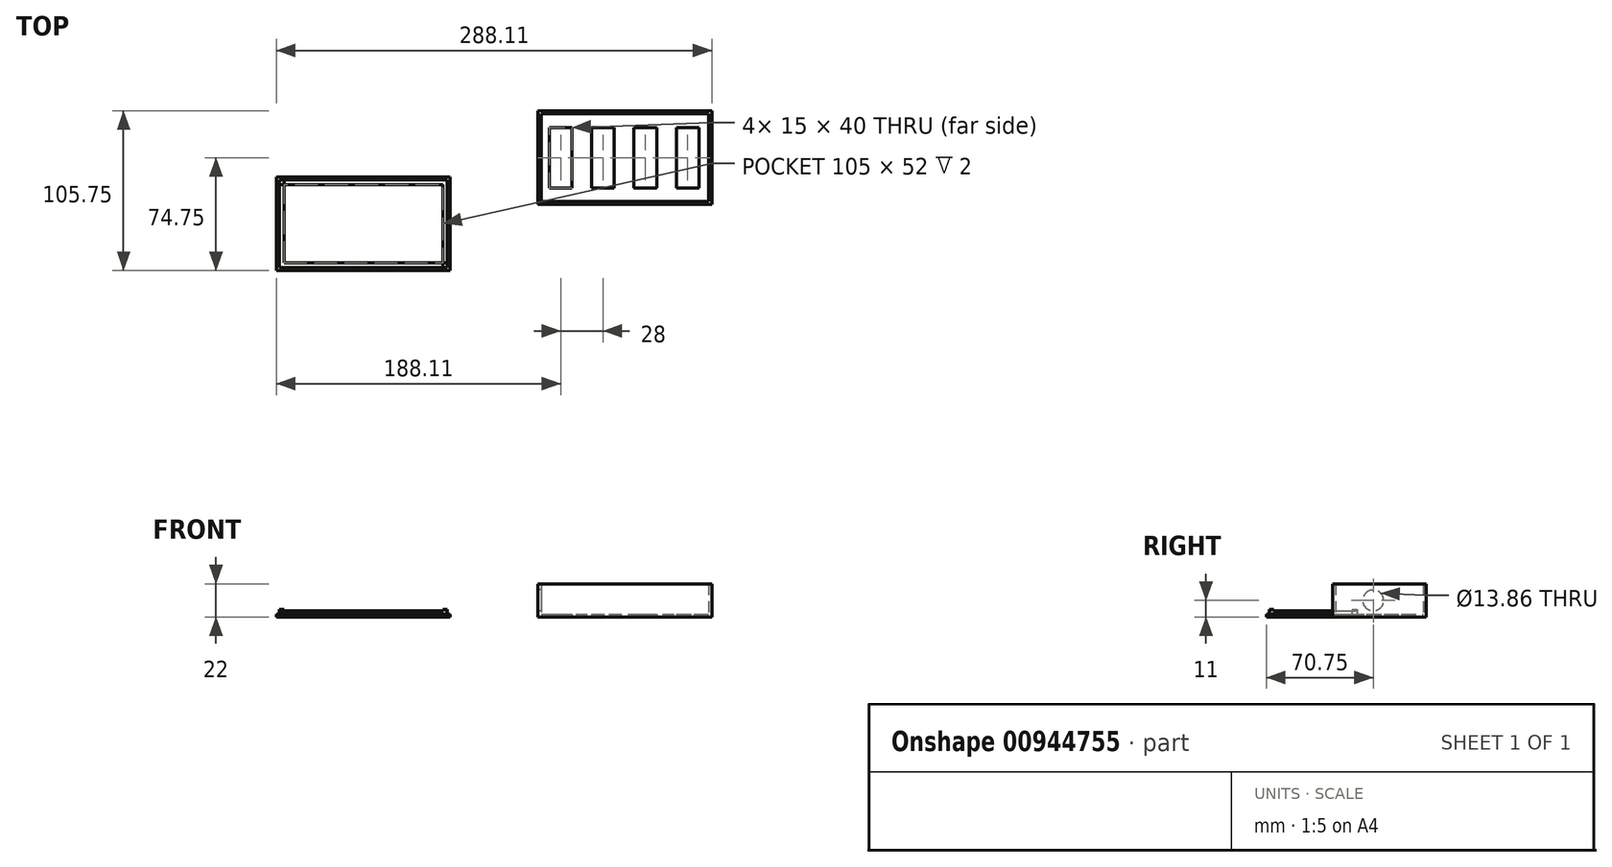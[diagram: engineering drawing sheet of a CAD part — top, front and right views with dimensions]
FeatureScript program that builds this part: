
annotation { "Feature Type Name" : "Feature", "Feature Type Description" : "" }
export const myFeature = defineFeature(function(context is Context, id is Id, definition is map)
    precondition{}
    {
        {
            var Q0;
            Q0=qCreatedBy(makeId("Top.planeOp"),FACE);
            var sketch = newSketch(context, id + "F0", { "sketchPlane" : qUnion([Q0])});
            skLineSegment(sketch, "E0.bottom", {"start": v(0, 0) * mm, "end": v(115, 0) * mm});
            skLineSegment(sketch, "E0.top", {"start": v(0, 62) * mm, "end": v(115, 62) * mm});
            skLineSegment(sketch, "E0.left", {"start": v(0, 0) * mm, "end": v(0, 62) * mm});
            skLineSegment(sketch, "E0.right", {"start": v(115, 0) * mm, "end": v(115, 62) * mm});
            skLineSegment(sketch, "E1.0", {"start": v(2, 2) * mm, "end": v(2, 60) * mm});
            skLineSegment(sketch, "E1.1", {"start": v(2, 2) * mm, "end": v(113, 2) * mm});
            skLineSegment(sketch, "E1.2", {"start": v(113, 2) * mm, "end": v(113, 60) * mm});
            skLineSegment(sketch, "E1.3", {"start": v(2, 60) * mm, "end": v(113, 60) * mm});
            skLineSegment(sketch, "E2.bottom", {"start": v(7.5, 11) * mm, "end": v(22.5, 11) * mm});
            skLineSegment(sketch, "E2.top", {"start": v(7.5, 51) * mm, "end": v(22.5, 51) * mm});
            skLineSegment(sketch, "E2.left", {"start": v(7.5, 11) * mm, "end": v(7.5, 51) * mm});
            skLineSegment(sketch, "E2.right", {"start": v(22.5, 11) * mm, "end": v(22.5, 51) * mm});
            skPoint(sketch, "E2.middle", {"position": v(15, 31) * mm});
            skPoint(sketch, "E2.middle.positionSnap0", {"position": v(2, 31) * mm});
            skPoint(sketch, "E2.centerSnap0", {"position": v(2, 31) * mm});
            skLineSegment(sketch, "E3.1.0.0", {"start": v(50.5, 11) * mm, "end": v(50.5, 51) * mm});
            skLineSegment(sketch, "E3.1.0.1", {"start": v(35.5, 11) * mm, "end": v(50.5, 11) * mm});
            skLineSegment(sketch, "E3.1.0.2", {"start": v(35.5, 11) * mm, "end": v(35.5, 51) * mm});
            skLineSegment(sketch, "E3.1.0.3", {"start": v(35.5, 51) * mm, "end": v(50.5, 51) * mm});
            skLineSegment(sketch, "E3.2.0.0", {"start": v(78.5, 11) * mm, "end": v(78.5, 51) * mm});
            skLineSegment(sketch, "E3.2.0.1", {"start": v(63.5, 11) * mm, "end": v(78.5, 11) * mm});
            skLineSegment(sketch, "E3.2.0.2", {"start": v(63.5, 11) * mm, "end": v(63.5, 51) * mm});
            skLineSegment(sketch, "E3.2.0.3", {"start": v(63.5, 51) * mm, "end": v(78.5, 51) * mm});
            skLineSegment(sketch, "E3.3.0.0", {"start": v(106.5, 11) * mm, "end": v(106.5, 51) * mm});
            skLineSegment(sketch, "E3.3.0.1", {"start": v(91.5, 11) * mm, "end": v(106.5, 11) * mm});
            skLineSegment(sketch, "E3.3.0.2", {"start": v(91.5, 11) * mm, "end": v(91.5, 51) * mm});
            skLineSegment(sketch, "E3.3.0.3", {"start": v(91.5, 51) * mm, "end": v(106.5, 51) * mm});
            skLineSegment(sketch, "E3.direction1", {"start": v(22.5, 11) * mm, "end": v(50.5, 11) * mm, "construction": true});
            skSolve(sketch);
        }
        {
            var Q0;
            Q0=makeQuery(id+"F0.imprint","IMPRINT",FACE,{"disambiguationData":[TD([[makeQuery(id+"F0.imprint","IMPRINT",EDGE,{"derivedFrom":sQuery(id+"F0.wireOp",EDGE,"E1.0")}),-1.0]])]});
            extrude(context, id + "F1", {"entities" : qUnion([Q0]), "depth" : 2 * mm, "offsetDistance" : 25 * mm});
        }
        {
            var Q0;
            Q0=makeQuery(id+"F0.imprint","IMPRINT",FACE,{"disambiguationData":[TD([[makeQuery(id+"F0.imprint","IMPRINT",EDGE,{"derivedFrom":sQuery(id+"F0.wireOp",EDGE,"E0.bottom")}),1.0]])]});
            extrude(context, id + "F2", {"entities" : qUnion([Q0]), "operationType" : NewBodyOperationType.ADD, "depth" : 22 * mm, "offsetDistance" : 25 * mm});
        }
        {
            var Q0;
            Q0=makeQuery(id+"F2.opExtrude","SWEPT_FACE",FACE,{"disambiguationData":[OSD([sQuery(id+"F0.wireOp",EDGE,"E0.left")])]});
            var sketch = newSketch(context, id + "F3", { "sketchPlane" : qUnion([Q0])});
            skCircle(sketch, "E4", {"center": v(-27, 11) * mm, "radius": 6.93 * mm});
            skPoint(sketch, "E4.centerSnap0", {"position": v(-62, 11) * mm});
            skSolve(sketch);
        }
        {
            var Q0;
            Q0=makeQuery(id+"F3.imprint","IMPRINT",FACE,{"disambiguationData":[TD([[makeQuery(id+"F3.imprint","IMPRINT",EDGE,{"derivedFrom":sQuery(id+"F3.wireOp",EDGE,"E4")}),1.0]])]});
            extrude(context, id + "F4", {"entities" : qUnion([Q0]), "operationType" : NewBodyOperationType.REMOVE, "oppositeDirection" : true, "depth" : 25 * mm, "offsetDistance" : 25 * mm});
        }
        {
            var Q0;
            Q0=qCreatedBy(makeId("Top.planeOp"),FACE);
            var sketch = newSketch(context, id + "F5", { "sketchPlane" : qUnion([Q0])});
            skLineSegment(sketch, "E5.bottom", {"start": v(-173.11, -43.75) * mm, "end": v(-58.11, -43.75) * mm});
            skLineSegment(sketch, "E5.top", {"start": v(-173.11, 18.25) * mm, "end": v(-58.11, 18.25) * mm});
            skLineSegment(sketch, "E5.left", {"start": v(-173.11, -43.75) * mm, "end": v(-173.11, 18.25) * mm});
            skLineSegment(sketch, "E5.right", {"start": v(-58.11, -43.75) * mm, "end": v(-58.11, 18.25) * mm});
            skLineSegment(sketch, "E6.0", {"start": v(-171.11, -41.75) * mm, "end": v(-171.11, 16.25) * mm});
            skLineSegment(sketch, "E6.1", {"start": v(-171.11, -41.75) * mm, "end": v(-60.11, -41.75) * mm});
            skLineSegment(sketch, "E6.2", {"start": v(-60.11, -41.75) * mm, "end": v(-60.11, 16.25) * mm});
            skLineSegment(sketch, "E6.3", {"start": v(-171.11, 16.25) * mm, "end": v(-60.11, 16.25) * mm});
            skPoint(sketch, "E7.middle.positionSnap0", {"position": v(-171.11, -12.75) * mm});
            skPoint(sketch, "E7.centerSnap0", {"position": v(-171.11, -12.75) * mm});
            skSolve(sketch);
        }
        {
            var Q0;
            Q0=makeQuery(id+"F5.imprint","IMPRINT",FACE,{"disambiguationData":[TD([[makeQuery(id+"F5.imprint","IMPRINT",EDGE,{"derivedFrom":sQuery(id+"F5.wireOp",EDGE,"E5.bottom")}),1.0]])]});
            extrude(context, id + "F6", {"entities" : qUnion([Q0]), "depth" : 2 * mm, "offsetDistance" : 25 * mm});
        }
        {
            var Q0;
            Q0=makeQuery(id+"F5.imprint","IMPRINT",FACE,{"disambiguationData":[TD([[makeQuery(id+"F5.imprint","IMPRINT",EDGE,{"derivedFrom":sQuery(id+"F5.wireOp",EDGE,"E6.0")}),-1.0]])]});
            extrude(context, id + "F7", {"entities" : qUnion([Q0]), "operationType" : NewBodyOperationType.ADD, "depth" : 4 * mm, "offsetDistance" : 25 * mm});
        }
        {
            var Q0;
            Q0=makeQuery(id+"F7.opExtrude","CAP_FACE",FACE,{"disambiguationData":[OSD([sQuery(id+"F5.wireOp",EDGE,"E6.0"),sQuery(id+"F5.wireOp",EDGE,"E6.1"),sQuery(id+"F5.wireOp",EDGE,"E6.2"),sQuery(id+"F5.wireOp",EDGE,"E6.3")])],"isStart":false});
            var sketch = newSketch(context, id + "F8", { "sketchPlane" : qUnion([Q0])});
            skLineSegment(sketch, "E8.0", {"start": v(-168.11, -38.75) * mm, "end": v(-168.11, 13.25) * mm});
            skLineSegment(sketch, "E8.1", {"start": v(-168.11, -38.75) * mm, "end": v(-63.11, -38.75) * mm});
            skLineSegment(sketch, "E8.2", {"start": v(-63.11, -38.75) * mm, "end": v(-63.11, 13.25) * mm});
            skLineSegment(sketch, "E8.3", {"start": v(-168.11, 13.25) * mm, "end": v(-63.11, 13.25) * mm});
            skLineSegment(sketch, "E9.bottom", {"start": v(-168.11, 13.25) * mm, "end": v(-171.11, 13.25) * mm});
            skLineSegment(sketch, "E9.top", {"start": v(-168.11, 16.25) * mm, "end": v(-171.11, 16.25) * mm});
            skLineSegment(sketch, "E9.left", {"start": v(-168.11, 13.25) * mm, "end": v(-168.11, 16.25) * mm});
            skLineSegment(sketch, "E9.right", {"start": v(-171.11, 13.25) * mm, "end": v(-171.11, 16.25) * mm});
            skLineSegment(sketch, "E10.bottom", {"start": v(-63.11, -38.75) * mm, "end": v(-60.11, -38.75) * mm});
            skLineSegment(sketch, "E10.top", {"start": v(-63.11, -41.75) * mm, "end": v(-60.11, -41.75) * mm});
            skLineSegment(sketch, "E10.left", {"start": v(-63.11, -38.75) * mm, "end": v(-63.11, -41.75) * mm});
            skLineSegment(sketch, "E10.right", {"start": v(-60.11, -38.75) * mm, "end": v(-60.11, -41.75) * mm});
            skSolve(sketch);
        }
        {
            var Q0;
            Q0=makeQuery(id+"F8.imprint","IMPRINT",FACE,{"disambiguationData":[TD([[makeQuery(id+"F8.imprint","IMPRINT",EDGE,{"derivedFrom":sQuery(id+"F8.wireOp",EDGE,"E8.0")}),-1.0]])]});
            extrude(context, id + "F9", {"entities" : qUnion([Q0]), "operationType" : NewBodyOperationType.REMOVE, "oppositeDirection" : true, "depth" : 2 * mm, "offsetDistance" : 25 * mm});
        }
        {
            var Q0;
            Q0=makeQuery(id+"F8.imprint","IMPRINT",FACE,{"disambiguationData":[TD([[makeQuery(id+"F8.imprint","IMPRINT",EDGE,{"derivedFrom":sQuery(id+"F8.wireOp",EDGE,"E10.bottom")}),-1.0]])]});
            var Q1;
            Q1=makeQuery(id+"F8.imprint","IMPRINT",FACE,{"disambiguationData":[TD([[makeQuery(id+"F8.imprint","IMPRINT",EDGE,{"derivedFrom":sQuery(id+"F8.wireOp",EDGE,"E9.bottom")}),-1.0]])]});
            extrude(context, id + "F10", {"entities" : qUnion([Q0, Q1]), "operationType" : NewBodyOperationType.ADD, "depth" : 1 * mm, "offsetDistance" : 25 * mm});
        }
    });
